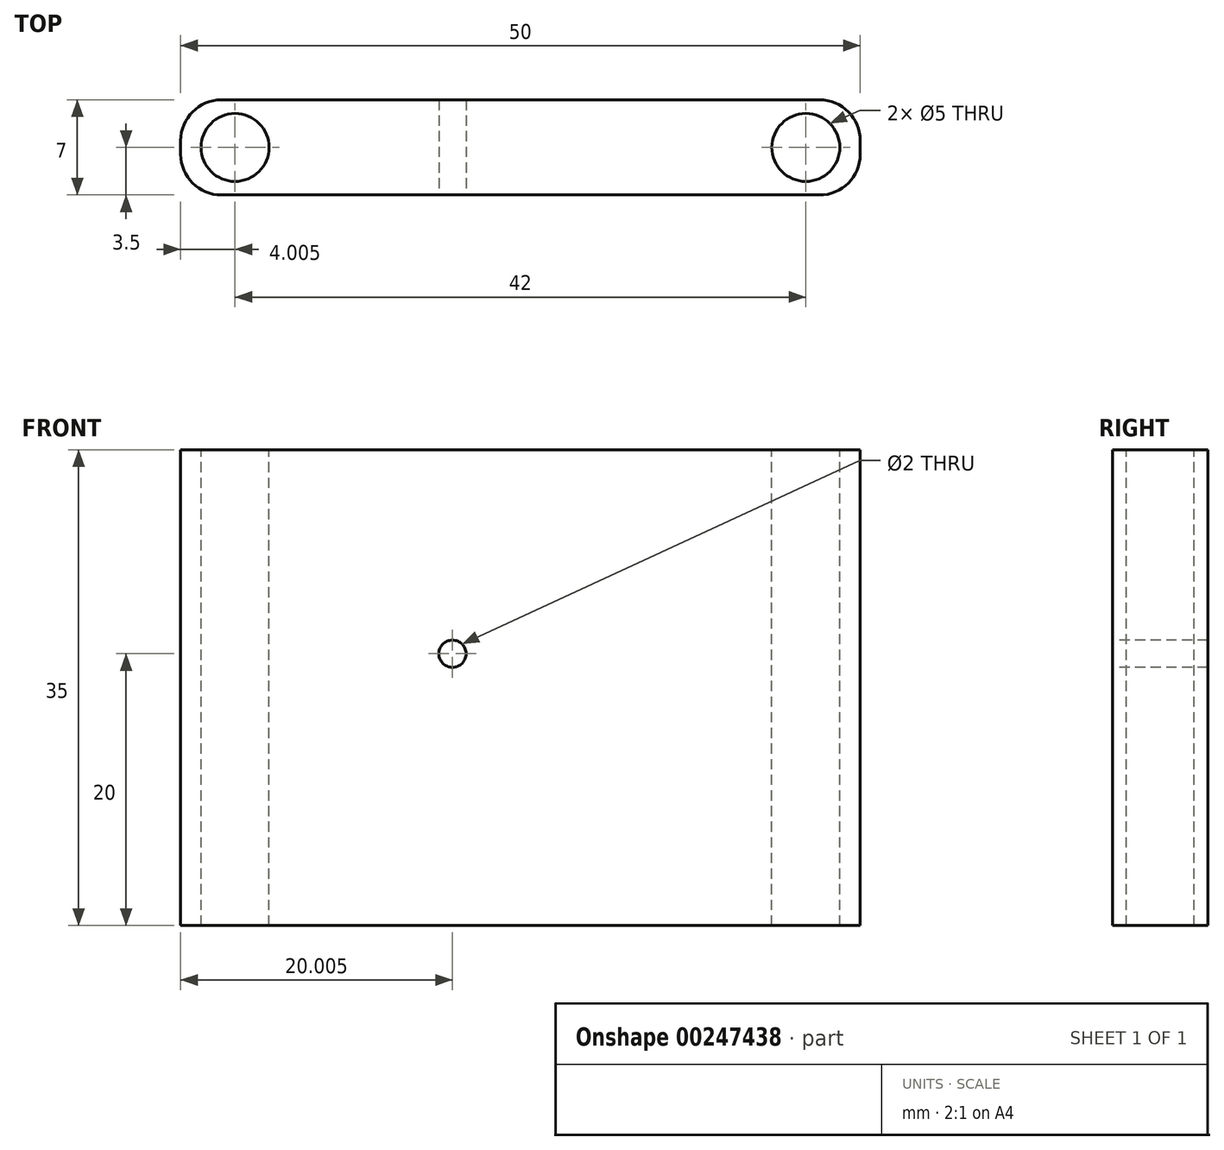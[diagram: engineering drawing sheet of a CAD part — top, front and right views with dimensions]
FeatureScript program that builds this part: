
annotation { "Feature Type Name" : "Feature", "Feature Type Description" : "" }
export const myFeature = defineFeature(function(context is Context, id is Id, definition is map)
    precondition{}
    {
        {
            var Q0;
            Q0=qCreatedBy(makeId("Top.planeOp"),FACE);
            var sketch = newSketch(context, id + "F0", { "sketchPlane" : qUnion([Q0])});
            skLineSegment(sketch, "E0.bottom", {"start": v(25.4, -3.5) * mm, "end": v(-24.6, -3.5) * mm});
            skLineSegment(sketch, "E0.top", {"start": v(25.4, 3.5) * mm, "end": v(-24.6, 3.5) * mm});
            skLineSegment(sketch, "E0.left", {"start": v(25.4, -3.5) * mm, "end": v(25.4, 3.5) * mm});
            skLineSegment(sketch, "E0.right", {"start": v(-24.6, -3.5) * mm, "end": v(-24.6, 3.5) * mm});
            skPoint(sketch, "E0.middle", {"position": v(0.4, 0) * mm});
            skSolve(sketch);
        }
        {
            var Q0;
            Q0 = qSketchRegion(id + "F0", true);
            extrude(context, id + "F1", {"entities" : qUnion([Q0]), "depth" : 35 * mm});
        }
        {
            var Q0;
            Q0=makeQuery(id+"F1.opExtrude","CAP_FACE",FACE,{"disambiguationData":[OSD([sQuery(id+"F0.wireOp",EDGE,"E0.bottom"),sQuery(id+"F0.wireOp",EDGE,"E0.top"),sQuery(id+"F0.wireOp",EDGE,"E0.left"),sQuery(id+"F0.wireOp",EDGE,"E0.right")])],"isStart":false});
            var sketch = newSketch(context, id + "F2", { "sketchPlane" : qUnion([Q0])});
            skCircle(sketch, "E1", {"center": v(-20.6, 0) * mm, "radius": 2.5 * mm});
            skCircle(sketch, "E2", {"center": v(21.4, 0) * mm, "radius": 2.5 * mm});
            skSolve(sketch);
        }
        {
            var Q0;
            Q0 = qSketchRegion(id + "F2", true);
            extrude(context, id + "F3", {"entities" : qUnion([Q0]), "operationType" : NewBodyOperationType.REMOVE, "endBound" : BoundingType.UP_TO_NEXT, "oppositeDirection" : true, "depth" : 25 * mm});
        }
        {
            var Q0;
            Q0=makeQuery(id+"F1.opExtrude","SWEPT_EDGE",EDGE,{"disambiguationData":[OSD([sQuery(id+"F0.wireOp",EDGE,"E0.bottom"),sQuery(id+"F0.wireOp",EDGE,"E0.left")])]});
            var Q1;
            Q1=makeQuery(id+"F1.opExtrude","SWEPT_EDGE",EDGE,{"disambiguationData":[OSD([sQuery(id+"F0.wireOp",EDGE,"E0.top"),sQuery(id+"F0.wireOp",EDGE,"E0.left")])]});
            var Q2;
            Q2=makeQuery(id+"F1.opExtrude","SWEPT_EDGE",EDGE,{"disambiguationData":[OSD([sQuery(id+"F0.wireOp",EDGE,"E0.bottom"),sQuery(id+"F0.wireOp",EDGE,"E0.right")])]});
            var Q3;
            Q3=makeQuery(id+"F1.opExtrude","SWEPT_EDGE",EDGE,{"disambiguationData":[OSD([sQuery(id+"F0.wireOp",EDGE,"E0.top"),sQuery(id+"F0.wireOp",EDGE,"E0.right")])]});
            fillet(context, id + "F4", {"entities" : qUnion([Q0, Q1, Q2, Q3]), "radius" : 3 * mm, "tangentPropagation" : true, "allowEdgeOverflow" : false});
        }
        {
            var Q0;
            Q0=makeQuery(id+"F1.opExtrude","SWEPT_FACE",FACE,{"disambiguationData":[OSD([sQuery(id+"F0.wireOp",EDGE,"E0.bottom")])]});
            var sketch = newSketch(context, id + "F5", { "sketchPlane" : qUnion([Q0])});
            skCircle(sketch, "E3", {"center": v(-4.6, 20) * mm, "radius": 1 * mm});
            skSolve(sketch);
        }
        {
            var Q0;
            Q0 = qSketchRegion(id + "F5", true);
            extrude(context, id + "F6", {"entities" : qUnion([Q0]), "operationType" : NewBodyOperationType.REMOVE, "oppositeDirection" : true, "depth" : 25 * mm});
        }
    });
